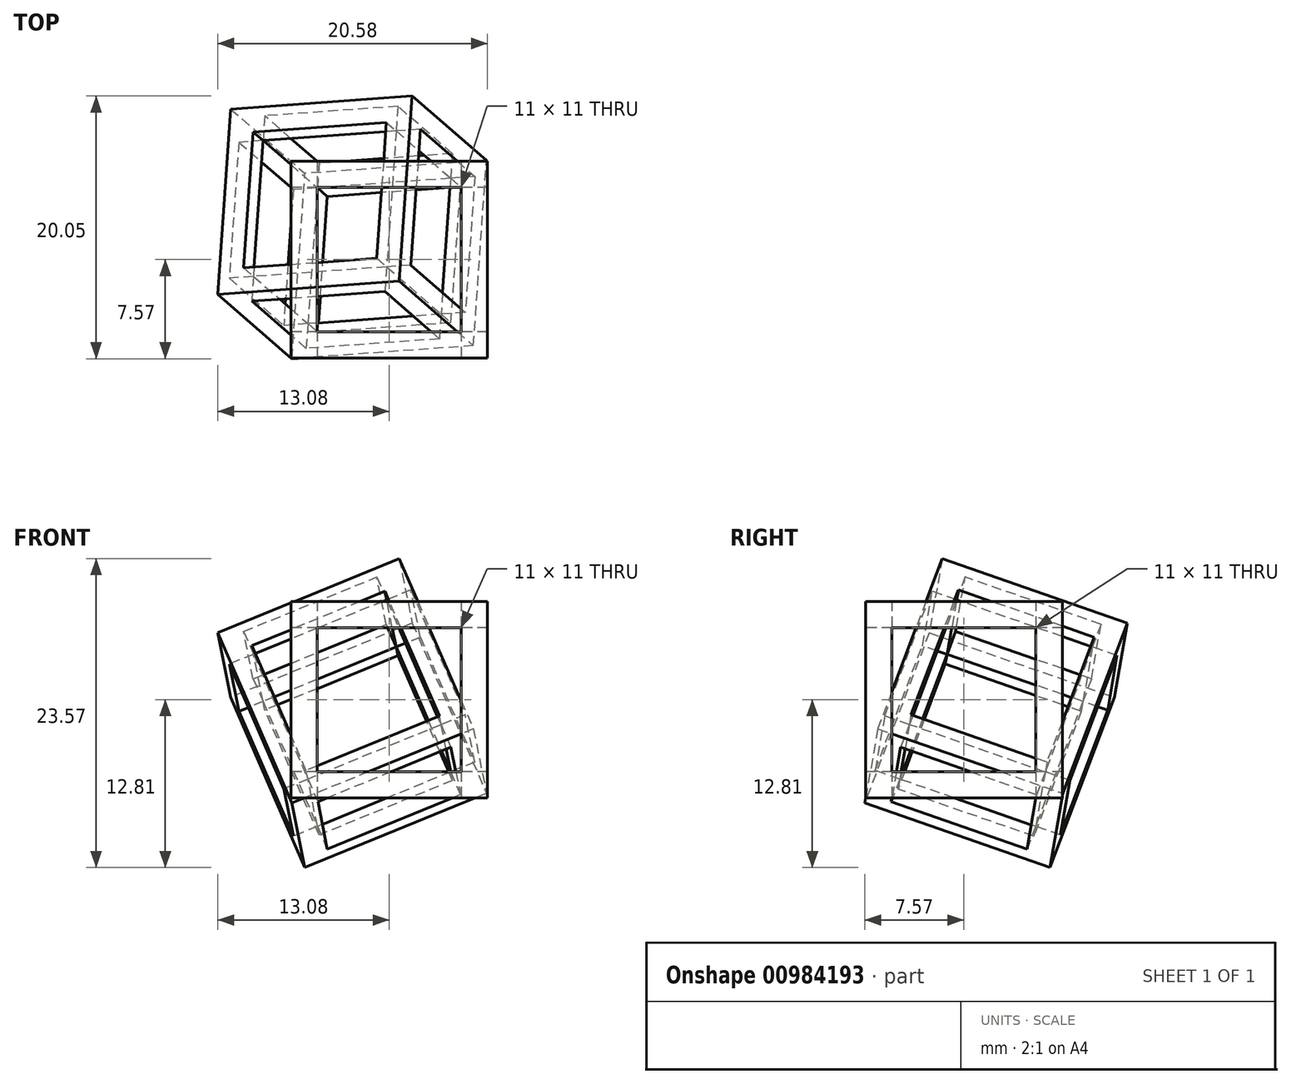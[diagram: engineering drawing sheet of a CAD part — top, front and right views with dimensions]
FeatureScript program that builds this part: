
annotation { "Feature Type Name" : "Feature", "Feature Type Description" : "" }
export const myFeature = defineFeature(function(context is Context, id is Id, definition is map)
    precondition{}
    {
        {
            var Q0;
            Q0=qCreatedBy(makeId("Top.planeOp"),FACE);
            var sketch = newSketch(context, id + "F0", { "sketchPlane" : qUnion([Q0])});
            skLineSegment(sketch, "E0.bottom", {"start": v(7.5, -7.5) * mm, "end": v(-7.5, -7.5) * mm});
            skLineSegment(sketch, "E0.top", {"start": v(7.5, 7.5) * mm, "end": v(-7.5, 7.5) * mm});
            skLineSegment(sketch, "E0.left", {"start": v(7.5, -7.5) * mm, "end": v(7.5, 7.5) * mm});
            skLineSegment(sketch, "E0.right", {"start": v(-7.5, -7.5) * mm, "end": v(-7.5, 7.5) * mm});
            skPoint(sketch, "E0.middle", {"position": v(0, 0) * mm});
            skLineSegment(sketch, "E1.bottom", {"start": v(5.5, -5.5) * mm, "end": v(-5.5, -5.5) * mm});
            skLineSegment(sketch, "E1.top", {"start": v(5.5, 5.5) * mm, "end": v(-5.5, 5.5) * mm});
            skLineSegment(sketch, "E1.left", {"start": v(5.5, -5.5) * mm, "end": v(5.5, 5.5) * mm});
            skLineSegment(sketch, "E1.right", {"start": v(-5.5, -5.5) * mm, "end": v(-5.5, 5.5) * mm});
            skLineSegment(sketch, "E2", {"start": v(1.58, 1.77) * mm, "end": v(-2.42, -2.84) * mm, "construction": true});
            skSolve(sketch);
        }
        {
            var Q0;
            Q0=makeQuery(id+"F0.imprint","IMPRINT",FACE,{"disambiguationData":[TD([[makeQuery(id+"F0.imprint","IMPRINT",EDGE,{"derivedFrom":sQuery(id+"F0.wireOp",EDGE,"E0.bottom")}),-1.0]])]});
            var Q1;
            Q1=makeQuery(id+"F0.imprint","IMPRINT",FACE,{"disambiguationData":[TD([[makeQuery(id+"F0.imprint","IMPRINT",EDGE,{"derivedFrom":sQuery(id+"F0.wireOp",EDGE,"E1.bottom")}),-1.0]])]});
            extrude(context, id + "F1", {"entities" : qUnion([Q0, Q1]), "depth" : 15 * mm, "offsetDistance" : 25 * mm});
        }
        {
            var Q0;
            Q0=makeQuery(id+"F0.imprint","IMPRINT",FACE,{"disambiguationData":[TD([[makeQuery(id+"F0.imprint","IMPRINT",EDGE,{"derivedFrom":sQuery(id+"F0.wireOp",EDGE,"E1.bottom")}),-1.0]])]});
            extrude(context, id + "F2", {"entities" : qUnion([Q0]), "operationType" : NewBodyOperationType.REMOVE, "endBound" : BoundingType.THROUGH_ALL, "depth" : 15 * mm, "offsetDistance" : 25 * mm});
        }
        {
            var Q0;
            Q0=makeQuery(id+"F1.opExtrude","SWEPT_FACE",FACE,{"disambiguationData":[OSD([sQuery(id+"F0.wireOp",EDGE,"E0.bottom")])]});
            var sketch = newSketch(context, id + "F3", { "sketchPlane" : qUnion([Q0])});
            skLineSegment(sketch, "E3.bottom", {"start": v(5.5, 2) * mm, "end": v(-5.5, 2) * mm});
            skLineSegment(sketch, "E3.top", {"start": v(5.5, 13) * mm, "end": v(-5.5, 13) * mm});
            skLineSegment(sketch, "E3.left", {"start": v(5.5, 2) * mm, "end": v(5.5, 13) * mm});
            skLineSegment(sketch, "E3.right", {"start": v(-5.5, 2) * mm, "end": v(-5.5, 13) * mm});
            skSolve(sketch);
        }
        {
            var Q0;
            Q0=makeQuery(id+"F3.imprint","IMPRINT",FACE,{"disambiguationData":[TD([[makeQuery(id+"F3.imprint","IMPRINT",EDGE,{"derivedFrom":sQuery(id+"F3.wireOp",EDGE,"E3.bottom")}),-1.0]])]});
            extrude(context, id + "F4", {"entities" : qUnion([Q0]), "operationType" : NewBodyOperationType.REMOVE, "endBound" : BoundingType.THROUGH_ALL, "oppositeDirection" : true, "depth" : 25 * mm, "offsetDistance" : 25 * mm});
        }
        {
            var Q0;
            Q0=makeQuery(id+"F1.opExtrude","SWEPT_FACE",FACE,{"disambiguationData":[OSD([sQuery(id+"F0.wireOp",EDGE,"E0.right")])]});
            var sketch = newSketch(context, id + "F5", { "sketchPlane" : qUnion([Q0])});
            skLineSegment(sketch, "E4.bottom", {"start": v(-5.5, 13) * mm, "end": v(5.5, 13) * mm});
            skLineSegment(sketch, "E4.top", {"start": v(-5.5, 2) * mm, "end": v(5.5, 2) * mm});
            skLineSegment(sketch, "E4.left", {"start": v(-5.5, 13) * mm, "end": v(-5.5, 2) * mm});
            skLineSegment(sketch, "E4.right", {"start": v(5.5, 13) * mm, "end": v(5.5, 2) * mm});
            skSolve(sketch);
        }
        {
            var Q0;
            Q0 = qSketchRegion(id + "F5", true);
            extrude(context, id + "F6", {"entities" : qUnion([Q0]), "operationType" : NewBodyOperationType.REMOVE, "endBound" : BoundingType.THROUGH_ALL, "oppositeDirection" : true, "depth" : 25 * mm, "offsetDistance" : 25 * mm});
        }
        {
            var Q0;
            Q0=makeQuery(id+"F1.opExtrude","SWEPT_BODY",BODY,{"disambiguationData":[OSD([sQuery(id+"F0.wireOp",EDGE,"E0.bottom"),sQuery(id+"F0.wireOp",EDGE,"E0.top"),sQuery(id+"F0.wireOp",EDGE,"E0.left"),sQuery(id+"F0.wireOp",EDGE,"E0.right")])]});
            var Q1;
            Q1=sQuery(id+"F0.wireOp",EDGE,"E2");
            transform(context, id + "F7", {"entities" : qUnion([Q0]), "transformType" : TransformType.ROTATION, "transformAxis" : qUnion([Q1]), "angle" : 30 * degree, "makeCopy" : true});
        }
    });
